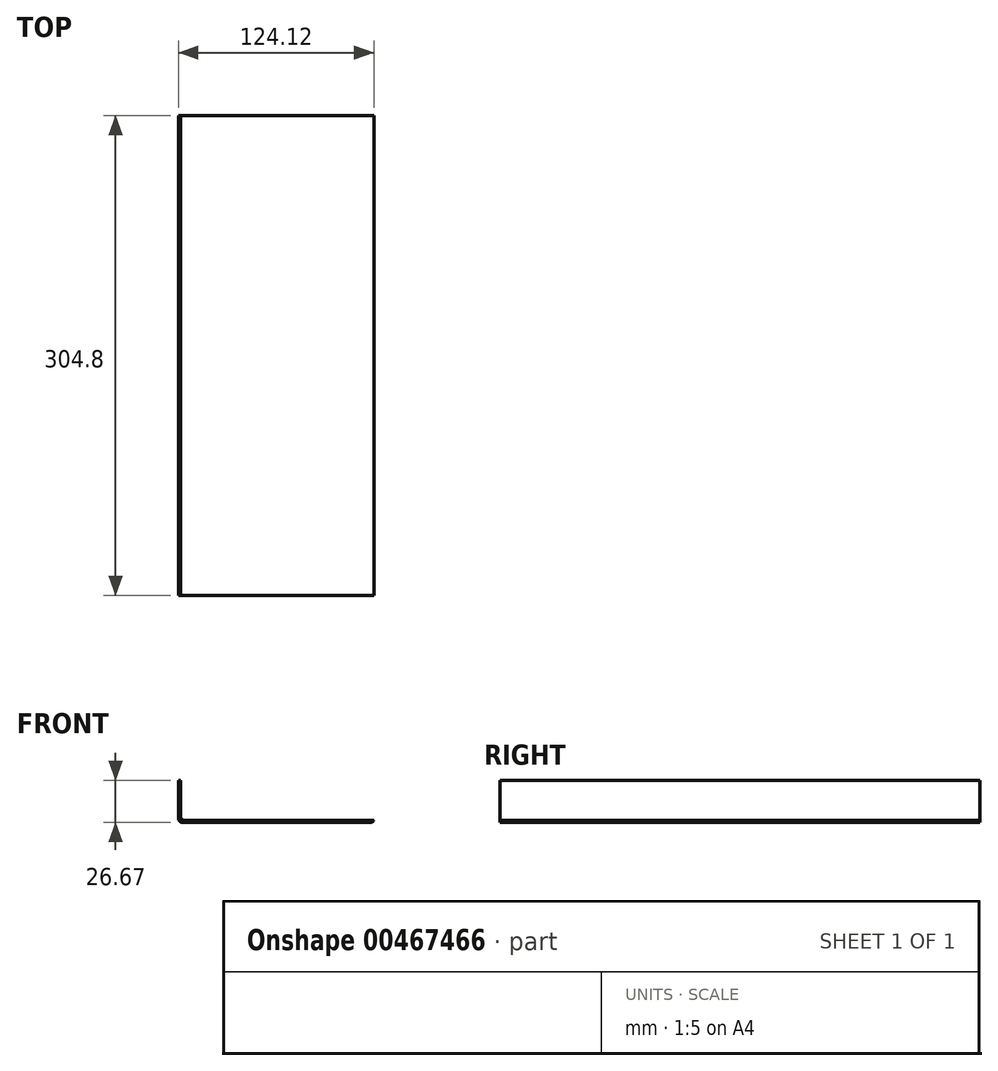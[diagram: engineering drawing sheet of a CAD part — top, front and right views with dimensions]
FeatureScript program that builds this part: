
annotation { "Feature Type Name" : "Feature", "Feature Type Description" : "" }
export const myFeature = defineFeature(function(context is Context, id is Id, definition is map)
    precondition{}
    {
        {
            var Q0;
            Q0=qCreatedBy(makeId("Front.planeOp"),FACE);
            var sketch = newSketch(context, id + "F0", { "sketchPlane" : qUnion([Q0])});
            skLineSegment(sketch, "E0", {"start": v(0, 0) * mm, "end": v(109.4, 0) * mm});
            skLineSegment(sketch, "E1", {"start": v(111.93, 2.54) * mm, "end": v(111.93, 26.67) * mm});
            skLineSegment(sketch, "E2", {"start": v(115.74, 26.67) * mm, "end": v(111.93, 26.67) * mm});
            skLineSegment(sketch, "E3", {"start": v(115.74, 26.67) * mm, "end": v(115.74, 3.81) * mm});
            skLineSegment(sketch, "E4", {"start": v(113.2, 1.27) * mm, "end": v(-8.72, 1.27) * mm});
            skLineSegment(sketch, "E5", {"start": v(-11.26, 3.81) * mm, "end": v(-11.26, 26.67) * mm});
            skLineSegment(sketch, "E6", {"start": v(-11.26, 26.67) * mm, "end": v(-12.53, 26.67) * mm});
            skLineSegment(sketch, "E7", {"start": v(-12.53, 26.67) * mm, "end": v(-12.53, 2.54) * mm});
            skLineSegment(sketch, "E8", {"start": v(-9.99, 0) * mm, "end": v(0, 0) * mm});
            skPoint(sketch, "E9.visualSharp", {"position": v(115.74, 1.27) * mm});
            skArc(sketch, "E9.filletArc", {"start": v(113.2, 1.27) * mm, "mid": v(115, 2.01) * mm, "end": v(115.74, 3.81) * mm});
            skPoint(sketch, "E10.visualSharp", {"position": v(111.93, 0) * mm});
            skArc(sketch, "E10.filletArc", {"start": v(109.4, 0) * mm, "mid": v(111.19, 0.74) * mm, "end": v(111.93, 2.54) * mm});
            skPoint(sketch, "E11.visualSharp", {"position": v(-11.26, 1.27) * mm});
            skArc(sketch, "E11.filletArc", {"start": v(-11.26, 3.81) * mm, "mid": v(-10.51, 2.01) * mm, "end": v(-8.72, 1.27) * mm});
            skPoint(sketch, "E12.visualSharp", {"position": v(-12.53, 0) * mm});
            skArc(sketch, "E12.filletArc", {"start": v(-12.53, 2.54) * mm, "mid": v(-11.78, 0.74) * mm, "end": v(-9.99, 0) * mm});
            skSolve(sketch);
        }
        {
            var Q0;
            Q0=makeQuery(id+"F0.imprint","IMPRINT",FACE,{"disambiguationData":[TD([[makeQuery(id+"F0.imprint","IMPRINT",EDGE,{"derivedFrom":sQuery(id+"F0.wireOp",EDGE,"E0")}),1.0]])]});
            extrude(context, id + "F1", {"entities" : qUnion([Q0]), "oppositeDirection" : true, "depth" : 304.8 * mm});
        }
    });
